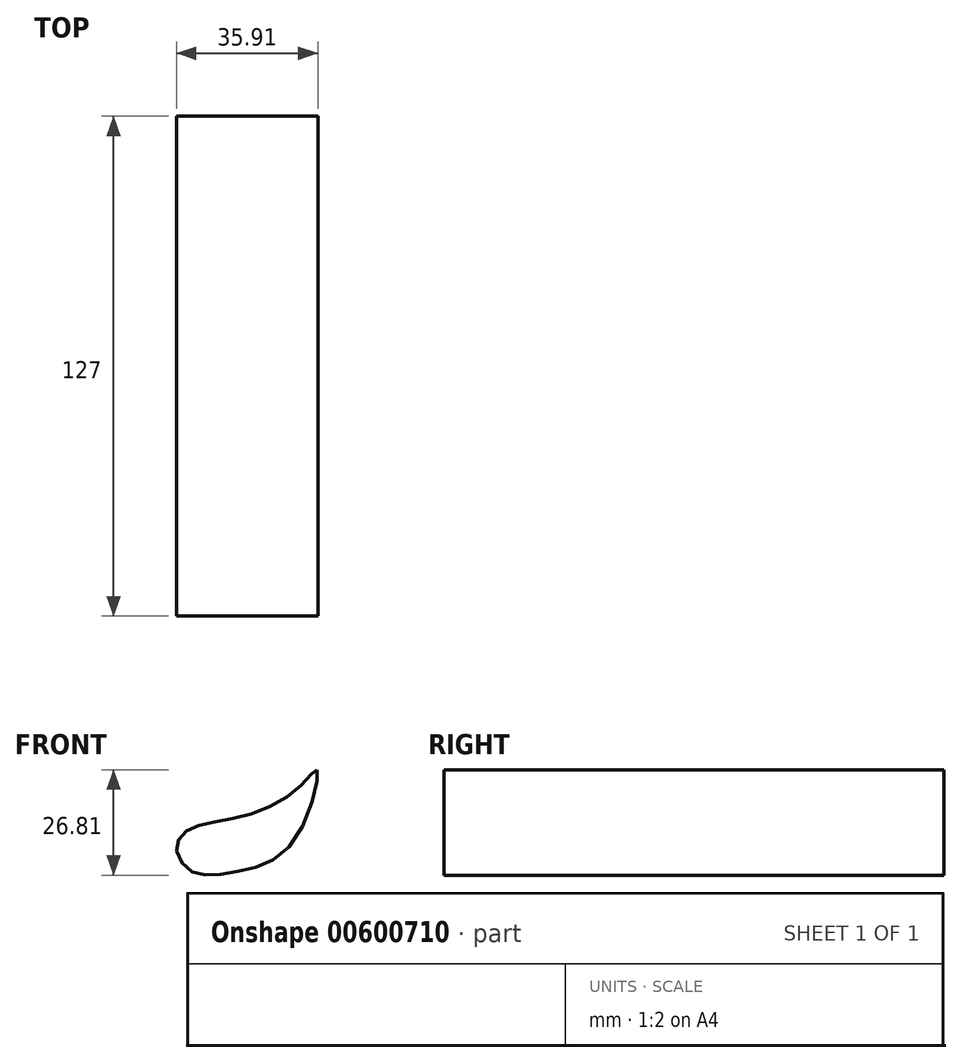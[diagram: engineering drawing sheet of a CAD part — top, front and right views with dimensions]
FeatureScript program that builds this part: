
annotation { "Feature Type Name" : "Feature", "Feature Type Description" : "" }
export const myFeature = defineFeature(function(context is Context, id is Id, definition is map)
    precondition{}
    {
        {
            var Q0;
            Q0=qCreatedBy(makeId("Front.planeOp"),FACE);
            var sketch = newSketch(context, id + "F0", { "sketchPlane" : qUnion([Q0])});
            skFitSpline(sketch, "E0", {"points": [v(0, 0) * mm, v(-4.27, -4.08) * mm, v(-19.24, -11.85) * mm, v(-32.14, -14.88) * mm, v(-35.74, -19.81) * mm, v(-31.76, -25.88) * mm, v(-21.14, -25.88) * mm, v(-6.16, -18.3) * mm, v(0, 0) * mm]});
            skSolve(sketch);
        }
        {
            var Q0;
            Q0 = qSketchRegion(id + "F0", true);
            extrude(context, id + "F1", {"entities" : qUnion([Q0]), "depth" : 127 * mm, "offsetDistance" : 25.4 * mm});
        }
    });
